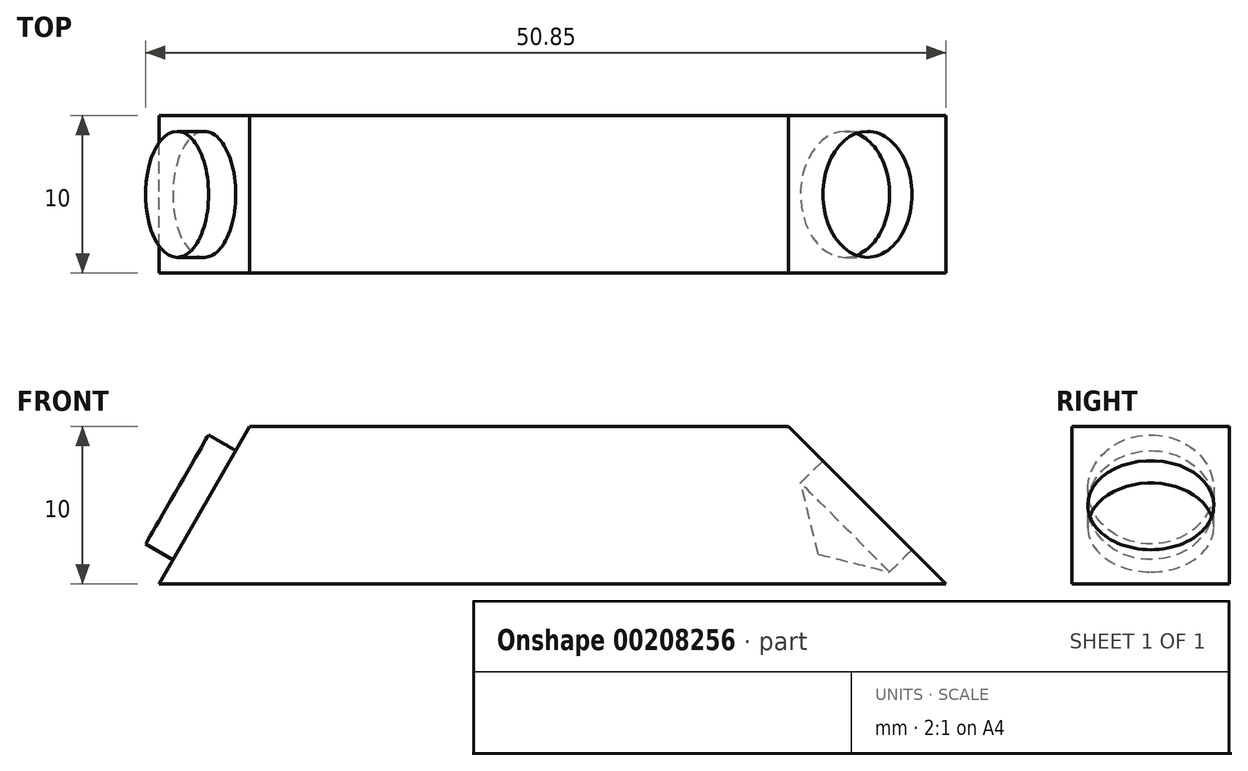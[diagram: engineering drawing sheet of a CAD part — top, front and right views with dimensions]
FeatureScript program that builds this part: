
annotation { "Feature Type Name" : "Feature", "Feature Type Description" : "" }
export const myFeature = defineFeature(function(context is Context, id is Id, definition is map)
    precondition{}
    {
        {
            var Q0;
            Q0=qCreatedBy(makeId("Top.planeOp"),FACE);
            var sketch = newSketch(context, id + "F0", { "sketchPlane" : qUnion([Q0])});
            skLineSegment(sketch, "E0", {"start": v(-41.18, 28.1) * mm, "end": v(8.82, 28.1) * mm});
            skLineSegment(sketch, "E1", {"start": v(8.82, 28.1) * mm, "end": v(8.82, 18.1) * mm});
            skLineSegment(sketch, "E2", {"start": v(8.82, 18.1) * mm, "end": v(-41.18, 18.1) * mm});
            skLineSegment(sketch, "E3", {"start": v(-41.18, 18.1) * mm, "end": v(-41.18, 28.1) * mm});
            skSolve(sketch);
        }
        {
            var Q0;
            Q0=makeQuery(id+"F0.imprint","IMPRINT",FACE,{"disambiguationData":[TD([[makeQuery(id+"F0.imprint","IMPRINT",EDGE,{"derivedFrom":sQuery(id+"F0.wireOp",EDGE,"E0")}),-1.0]])]});
            extrude(context, id + "F1", {"entities" : qUnion([Q0]), "depth" : 10 * mm});
        }
        {
            var Q0;
            Q0=makeQuery(id+"F1.opExtrude","CAP_EDGE",EDGE,{"disambiguationData":[OSD([sQuery(id+"F0.wireOp",EDGE,"E1")])],"isStart":false});
            chamfer(context, id + "F2", {"entities" : qUnion([Q0]), "width" : 10 * mm, "tangentPropagation" : true});
        }
        {
            var Q0;
            Q0=makeQuery(id+"F2.opChamfer","BLEND_FACE",FACE,{"disambiguationData":[OSD([sQuery(id+"F0.wireOp",EDGE,"E1")])]});
            var sketch = newSketch(context, id + "F3", { "sketchPlane" : qUnion([Q0])});
            skCircle(sketch, "E4", {"center": v(23.1, 0.84) * mm, "radius": 4 * mm});
            skSolve(sketch);
        }
        {
            var Q0;
            Q0=sQuery(id+"F3.wireOp",VERTEX,"E4.center");
            var Q1;
            Q1=makeQuery(id+"F1.opExtrude","SWEPT_BODY",BODY,{"disambiguationData":[OSD([sQuery(id+"F0.wireOp",EDGE,"E0"),sQuery(id+"F0.wireOp",EDGE,"E1"),sQuery(id+"F0.wireOp",EDGE,"E2"),sQuery(id+"F0.wireOp",EDGE,"E3")])]});
            hole(context, id + "F4", {"style" : HoleStyle.SIMPLE, "endStyle" : HoleEndStyle.BLIND, "holeDiameter" : 8 * mm, "holeDepth" : 2 * mm, "locations" : qUnion([Q0]), "scope" : qUnion([Q1])});
        }
        {
            var Q0;
            Q0=makeQuery(id+"F1.opExtrude","CAP_EDGE",EDGE,{"disambiguationData":[OSD([sQuery(id+"F0.wireOp",EDGE,"E3")])],"isStart":false});
            chamfer(context, id + "F5", {"entities" : qUnion([Q0]), "chamferType" : ChamferType.OFFSET_ANGLE, "width" : 10 * mm, "oppositeDirection" : false, "angle" : 30 * degree, "tangentPropagation" : true});
        }
        {
            var Q0;
            Q0=makeQuery(id+"F5.opChamfer","BLEND_FACE",FACE,{"disambiguationData":[OSD([sQuery(id+"F0.wireOp",EDGE,"E3")])]});
            var sketch = newSketch(context, id + "F6", { "sketchPlane" : qUnion([Q0])});
            skCircle(sketch, "E5", {"center": v(-23.1, -14.82) * mm, "radius": 4 * mm});
            skSolve(sketch);
        }
        {
            var Q0;
            Q0=makeQuery(id+"F6.imprint","IMPRINT",FACE,{"disambiguationData":[TD([[makeQuery(id+"F6.imprint","IMPRINT",EDGE,{"derivedFrom":sQuery(id+"F6.wireOp",EDGE,"E5")}),1.0]])]});
            extrude(context, id + "F7", {"entities" : qUnion([Q0]), "operationType" : NewBodyOperationType.ADD, "depth" : 2 * mm});
        }
    });
